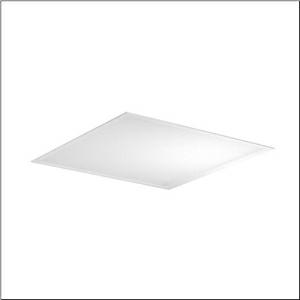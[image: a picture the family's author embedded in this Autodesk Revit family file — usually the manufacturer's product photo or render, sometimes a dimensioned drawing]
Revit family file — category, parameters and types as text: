
# Revit family: apollon_21_square_51mq12w72m14
name_source: partatom
category: Lighting Fixtures
units: mm (PartAtom-declared; Revit-internal decimal feet)

## family parameters
Cut with Voids When Loaded = No
Host = Face
Light Source = No
Part Type = Normal
Room Calculation Point = No
Round Connector Dimension = Use Diameter
Shared = No

## types (1)
- --- (1 x LED, 4200 lm, 24.2 W, 4000K)
    Apparent Load = 24 VA
    CIE Flux Codes = 60 87 97 100 100
    Color Rendering = 80
    Color Temperature = 4000K
    Default Elevation = 1800 mm
    Description = Apollon 21 square, office luminaire, primary optical cover: micro prismatic cover, of PMMA, CAT 2 (L<= 3000cd/m²), light emission: direct distribution, primary light characteristic: symmetric, installation type: lay-in mounting, recessed, LED, rated luminous flux: 4.200lm, luminous efficacy: 174lm/W, light colour: 830/840, colour temperature: 3000/4000K, control gear: ON/OFF, with terminal, 3-pole, mains connection: 220..240V, AC/DC, 0/50..60Hz, rated input power: 24.2W, suitable for self-contained emergency lighting element 59MQE002602A with integrated self-test function according to EN 60598-2-22, housing, of aluminium, coated, traffic white (RAL 9016), module: M600, length: 595mm, width: 595mm, height: 55mm, housing upper side, of sheet steel, galvanised, protection rating (complete): IP20, protection rating (lamp compartment, on room side): IP50, insulation class (complete): insulation class II (safety insulation), certification: CE, ENEC, impact resistance: IK03, permissible operating ambient temperature: -20..+45°C, standard: EN 60598-2-22, corresponds to IFS (International Featured Standards) requirements for safety and quality in the food industry, packaging unit: 1 piece
    Height = 0 mm  [stored 0 ft]
    Lamp = 1 x LED
    Lamp Light Flux = 4200 lm
    Lamp Power = 24.2 W
    Lamp count = 1
    Length = 595 mm
    Luminous efficacy = 174 lm/W
    Manufacturer = Siteco
    ModVariant = No
    Model = 51MQ12W72M14
    Mounting Place = Ceiling
    Mounting Type = Recessed
    Number of Poles = 1
    OnlyDefault = Yes
    Power Factor = 1
    Product Name = Apollon 21 square
    Product group = office luminaire | ceiling recessed
    ProductGroupID = 400
    Protection Class = Protection class II
    Protection Degree = IP 20
    RLX_Detail_Level = 1
    RLX_Emergency_Light_Flux = 0 lm
    RLX_Emergency_Type = 0
    RLX_Emergency_Type_DB = No
    RlxData = <blob elided: 97101 chars, md5=837a8f33>
    Socket = socket
    Standby Power = 0 W
    System Light Flux = 4200 lm
    System Power = 24 W
    Type Comments = factory setting
    Type Image = l_1291049.jpg
    URL = http://relux.com
    VarID = @adj_075915
    Voltage = 0 V
    Weight = 0.00 kg
    Width = 595 mm

note: [stored X ft] marks values corroborated as IEEE doubles in the binary element streams (Revit-internal decimal feet)

## geometry (parser evidence)
native form markers: Blend x4, Sweep x9
no freeform markers — native parametric forms only
